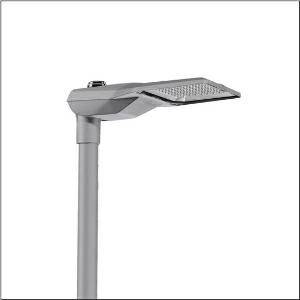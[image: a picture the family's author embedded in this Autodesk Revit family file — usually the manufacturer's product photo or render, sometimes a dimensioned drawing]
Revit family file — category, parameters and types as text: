
# Revit family: streetlight_sl_21_midi___stw1_0a_5xe7e47n08mb_f37a
name_source: partatom
category: Lighting Fixtures
units: mm (PartAtom-declared; Revit-internal decimal feet)

## family parameters
Cut with Voids When Loaded = No
Host = Face
Light Source = No
Part Type = Normal
Room Calculation Point = No
Round Connector Dimension = Use Diameter
Shared = No

## types (1)
- --- (1 x LED, 20180 lm, 147 W, 4000K)
    Apparent Load = 147 VA
    CIE Flux Codes = 38 75 98 100 100
    Color Rendering = 70
    Color Temperature = 4000K
    Default Elevation = 1800 mm
    Description = Streetlight SL 21 midi, mast luminaire, primary light control with lens, of PMMA, primary optical cover: cover, of toughened safety glass, transparent, light distribution: STW1.0a, light emission: direct distribution, primary light characteristic: asymmetric, installation type: side-entry, LED, 3G 2.5mm², High Power LED, rated luminous flux: 20.180lm, luminous efficacy: 137lm/W, light colour: 740, colour temperature: 4000K, control: overheat protection, presetting dimming linear, constant luminous flux control, time-dependent luminous flux control, flexible luminous flux parameterisation, mains connection: 220..240V, AC, 50/60Hz, connection cable pre-assembled, cable length: 12,5m, wiring characteristics: H05VV-F, start of lifetime: 147W, end of service life: 155W, reduction: 65W, luminaire housing, of diecast aluminium (EN AC-44300), powder-coated, Siteco® metallic grey (DB 702S), corrosivity category C5 mid according to DIN EN ISO 12944, multi-level sealing system, sealing non-destructively replaceable, inclination adjustable: 0°, 5°, 10°, 15°, length: 644mm, width: 335mm, height: 110mm, spigot size: 42mm (side-entry), protection rating (complete): IP66, insulation class (complete): insulation class I (protective earthing), certification: CE, ENEC, ENEC+, VDE, impact resistance: IK09, permissible operating ambient temperature for outdoor applications: -40..+50°C, standard-compliant lighting for roads and squares, packaging unit: 1 piece

Light Distribution: STW1.0a
    Height = 111 mm
    Lamp = 1 x LED
    Lamp Light Flux = 20180 lm
    Lamp Power = 147 W
    Lamp count = 1
    Length = 644 mm
    Luminous efficacy = 137 lm/W
    Manufacturer = Siteco
    ModVariant = No
    Model = 5XE7E47N08MB
    Number of Poles = 1
    OnlyDefault = Yes
    Power Factor = 1
    Product Name = Streetlight SL 21 midi | STW1.0a
    Product group = mast luminaire | pylon top
    ProductGroupID = 6100
    Protection Class = Protection class I
    Protection Degree = IP 66
    RLX_Detail_Level = 1
    RLX_Emergency_Light_Flux = 0 lm
    RLX_Emergency_Type = 0
    RLX_Emergency_Type_DB = No
    RlxData = <blob elided: 91657 chars, md5=01dbb69e>
    Socket = socket
    Standby Power = 0 W
    System Light Flux = 20180 lm
    System Power = 147 W
    Type Comments = factory setting: luminous flux: 100 % | dim-lin: 254 | 750 mA
    Type Image = l_1294377.jpg
    URL = http://relux.com
    VarID = @adj_084819
    Voltage = 0 V
    Weight = 0.00 kg
    Width = 336 mm

## geometry (parser evidence)
native form markers: Blend x4, Sweep x11
no freeform markers — native parametric forms only
